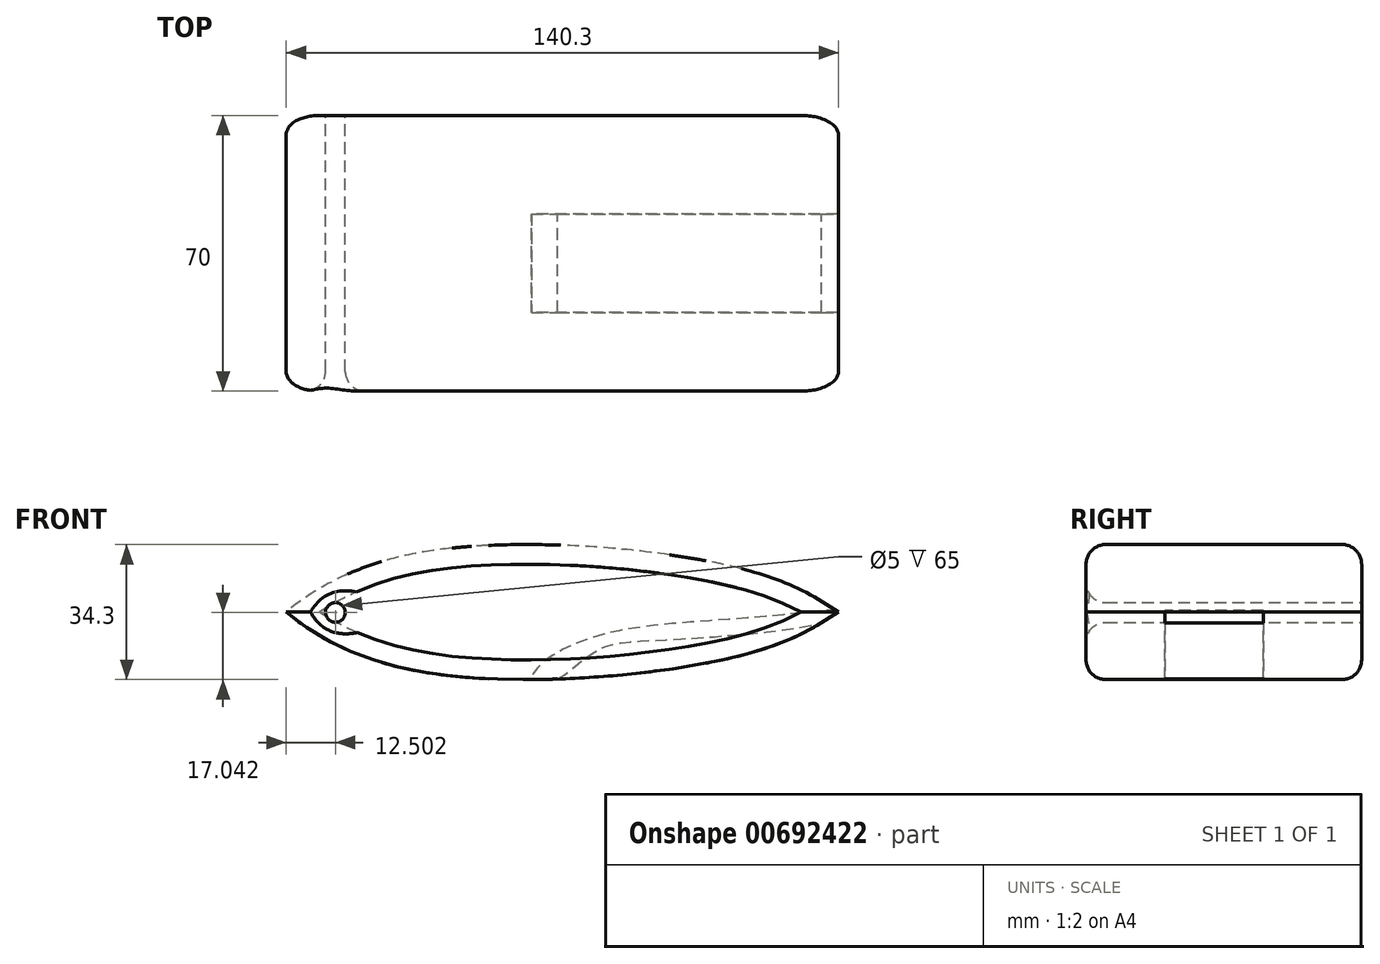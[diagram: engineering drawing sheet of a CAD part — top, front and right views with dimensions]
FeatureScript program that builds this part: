
annotation { "Feature Type Name" : "Feature", "Feature Type Description" : "" }
export const myFeature = defineFeature(function(context is Context, id is Id, definition is map)
    precondition{}
    {
        {
            var Q0;
            Q0=qCreatedBy(makeId("Front.planeOp"),FACE);
            var sketch = newSketch(context, id + "F0", { "sketchPlane" : qUnion([Q0])});
            skLineSegment(sketch, "E0", {"start": v(-69.2, 0) * mm, "end": v(71.1, 0) * mm});
            skFitSpline(sketch, "E1", {"points": [v(-69.2, 0) * mm, v(-32.88, 15.5) * mm, v(49.79, 10.12) * mm, v(71.1, 0) * mm], "startDerivative": vector(77.96, 64.4) * mm, "endDerivative": vector(61.48, -40.06) * mm});
            skFitSpline(sketch, "E2.MirrorCS", {"points": [v(-69.2, 0) * mm, v(-32.88, -15.5) * mm, v(49.79, -10.12) * mm, v(71.1, 0) * mm], "startDerivative": vector(77.96, -64.4) * mm, "endDerivative": vector(61.48, 40.06) * mm});
            skSolve(sketch);
        }
        {
            var Q0;
            Q0 = qSketchRegion(id + "F0", true);
            extrude(context, id + "F1", {"entities" : qUnion([Q0]), "depth" : 70 * mm, "offsetDistance" : 25 * mm});
        }
        {
            var Q0;
            Q0=makeQuery(id+"F1.opExtrude","CAP_FACE",FACE,{"disambiguationData":[OSD([sQuery(id+"F0.wireOp",EDGE,"E1"),sQuery(id+"F0.wireOp",EDGE,"E2.MirrorCS")])],"isStart":true});
            var sketch = newSketch(context, id + "F2", { "sketchPlane" : qUnion([Q0])});
            skCircle(sketch, "E3", {"center": v(56.7, -0.1) * mm, "radius": 2.5 * mm});
            skPoint(sketch, "E3.first.point", {"position": v(55.58, 2.13) * mm});
            skPoint(sketch, "E3.second.point", {"position": v(58.53, -1.8) * mm});
            skPoint(sketch, "E3.third.point", {"position": v(57.95, -2.27) * mm});
            skSolve(sketch);
        }
        {
            var Q0;
            Q0 = qSketchRegion(id + "F2", true);
            extrude(context, id + "F3", {"entities" : qUnion([Q0]), "operationType" : NewBodyOperationType.REMOVE, "oppositeDirection" : true, "depth" : 100 * mm, "offsetDistance" : 25 * mm, "hasSecondDirection" : true, "secondDirectionOppositeDirection" : false, "secondDirectionDepth" : 72.9 * mm});
        }
        {
            var Q0;
            Q0=makeQuery(id+"F1.opExtrude","CAP_FACE",FACE,{"disambiguationData":[OSD([sQuery(id+"F0.wireOp",EDGE,"E1"),sQuery(id+"F0.wireOp",EDGE,"E2.MirrorCS")])],"isStart":true});
            var Q1;
            Q1=makeQuery(id+"F1.opExtrude","CAP_FACE",FACE,{"disambiguationData":[OSD([sQuery(id+"F0.wireOp",EDGE,"E1"),sQuery(id+"F0.wireOp",EDGE,"E2.MirrorCS")])],"isStart":false});
            fillet(context, id + "F4", {"entities" : qUnion([Q0, Q1]), "radius" : 5 * mm, "tangentPropagation" : true, "allowEdgeOverflow" : false});
        }
        {
            var Q0;
            Q0=makeQuery(id+"F0.imprint","IMPRINT",FACE,{"disambiguationData":[TD([[makeQuery(id+"F0.imprint","IMPRINT",EDGE,{"derivedFrom":sQuery(id+"F0.wireOp",EDGE,"E0")}),-1.0]])]});
            var sketch = newSketch(context, id + "F5", { "sketchPlane" : qUnion([Q0])});
            skFitSpline(sketch, "E4", {"points": [v(71.01, 0) * mm, v(53.1, -1.12) * mm, v(12.92, -5.28) * mm, v(-5.01, -13.8) * mm, v(-6.7, -17.66) * mm, v(-1.36, -17.56) * mm, v(9.32, -9.98) * mm, v(25.66, -7.1) * mm, v(68.63, -2.12) * mm, v(71.01, 0) * mm]});
            skSolve(sketch);
        }
        {
            var Q0;
            Q0 = qSketchRegion(id + "F5", true);
            extrude(context, id + "F6", {"entities" : qUnion([Q0]), "operationType" : NewBodyOperationType.REMOVE, "depth" : 50 * mm, "offsetDistance" : 25 * mm, "hasSecondDirection" : true, "secondDirectionOppositeDirection" : true, "secondDirectionDepth" : 25 * mm});
        }
        {
            var Q0;
            Q0=makeQuery(id+"F0.imprint","IMPRINT",FACE,{"disambiguationData":[TD([[makeQuery(id+"F0.imprint","IMPRINT",EDGE,{"derivedFrom":sQuery(id+"F0.wireOp",EDGE,"E0")}),-1.0]])]});
            extrude(context, id + "F7", {"entities" : qUnion([Q0]), "operationType" : NewBodyOperationType.ADD, "depth" : 25 * mm, "offsetDistance" : 25 * mm});
        }
        {
            var Q0;
            Q0=makeQuery(id+"F0.imprint","IMPRINT",FACE,{"disambiguationData":[TD([[makeQuery(id+"F0.imprint","IMPRINT",EDGE,{"derivedFrom":sQuery(id+"F0.wireOp",EDGE,"E0")}),1.0]])]});
            extrude(context, id + "F8", {"entities" : qUnion([Q0]), "operationType" : NewBodyOperationType.ADD, "depth" : 25 * mm, "offsetDistance" : 25 * mm});
        }
        {
            var Q0;
            Q0=makeQuery(id+"F2.imprint","IMPRINT",FACE,{"disambiguationData":[TD([[makeQuery(id+"F2.imprint","IMPRINT",EDGE,{"derivedFrom":sQuery(id+"F2.wireOp",EDGE,"E3")}),1.0]])]});
            extrude(context, id + "F9", {"entities" : qUnion([Q0]), "operationType" : NewBodyOperationType.REMOVE, "oppositeDirection" : true, "depth" : 70 * mm, "offsetDistance" : 25 * mm});
        }
        {
            var Q0;
            Q0=makeQuery(id+"F9.boolean.opBoolean","COPY",EDGE,{"derivedFrom":makeQuery(id+"F9.opExtrude","CAP_EDGE",EDGE,{"disambiguationData":[OSD([sQuery(id+"F2.wireOp",EDGE,"E3")])],"isStart":true})});
            var Q1;
            Q1=makeQuery(id+"F8.opExtrude","CAP_EDGE",EDGE,{"disambiguationData":[OSD([sQuery(id+"F0.wireOp",EDGE,"E1")])],"isStart":true});
            var Q2;
            Q2=makeQuery(id+"F7.opExtrude","CAP_EDGE",EDGE,{"disambiguationData":[OSD([sQuery(id+"F0.wireOp",EDGE,"E2.MirrorCS")])],"isStart":true});
            fillet(context, id + "F10", {"entities" : qUnion([Q0, Q1, Q2]), "radius" : 5 * mm, "tangentPropagation" : true, "allowEdgeOverflow" : false});
        }
    });
